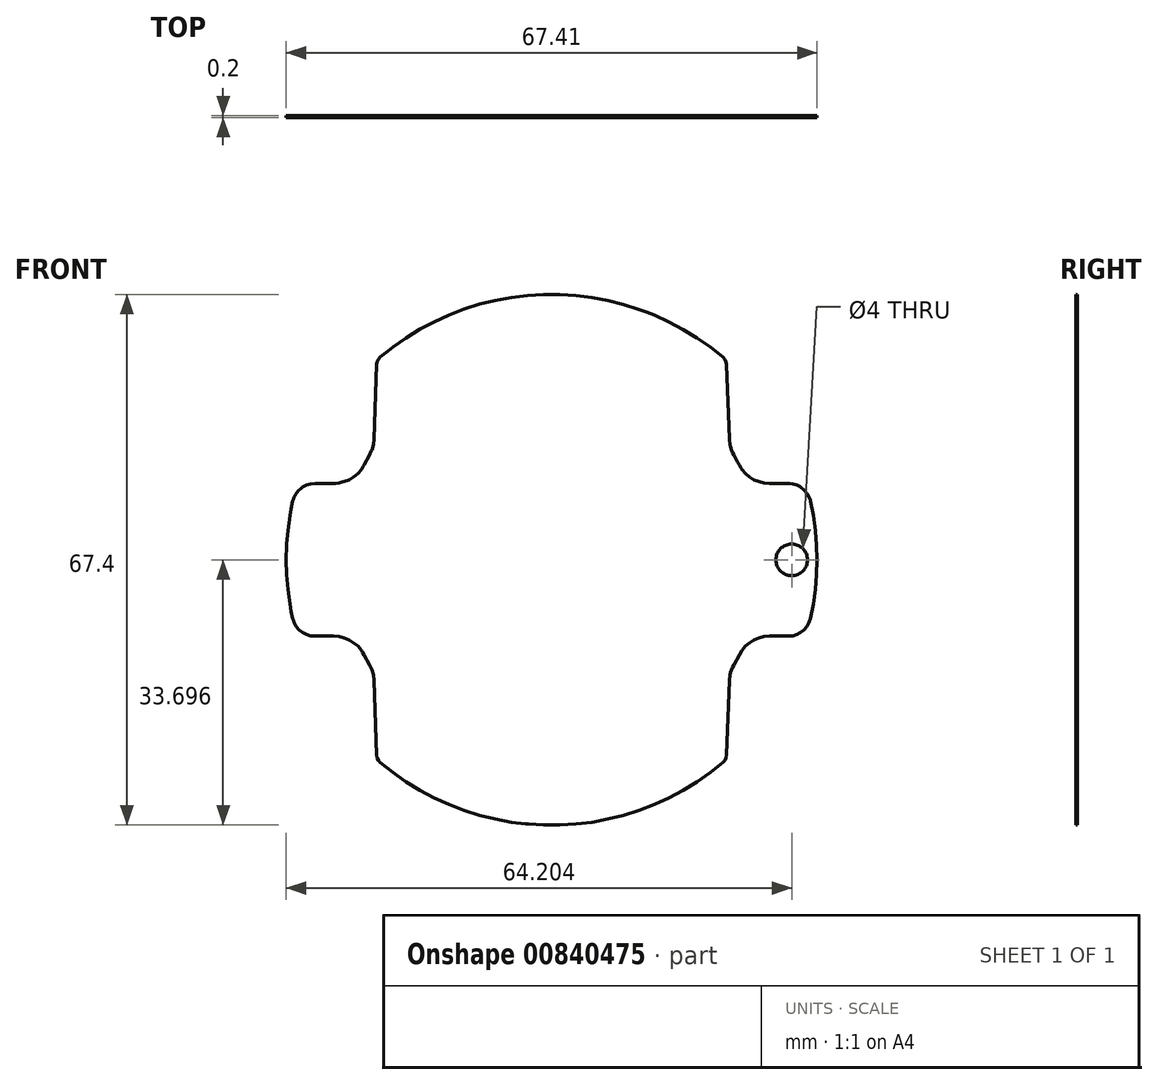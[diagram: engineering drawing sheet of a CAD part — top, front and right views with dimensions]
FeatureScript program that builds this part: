
annotation { "Feature Type Name" : "Feature", "Feature Type Description" : "" }
export const myFeature = defineFeature(function(context is Context, id is Id, definition is map)
    precondition{}
    {
        {
            var Q0;
            Q0=qCreatedBy(makeId("Front.planeOp"),FACE);
            var sketch = newSketch(context, id + "F0", { "sketchPlane" : qUnion([Q0])});
            skFitSpline(sketch, "E0.0.0", {"points": [v(23.84, -14.54) * mm, v(23.9, -14.43) * mm, v(23.95, -14.32) * mm, v(24, -14.2) * mm]});
            skFitSpline(sketch, "E0.0.1", {"points": [v(24, -14.2) * mm, v(24.24, -13.78) * mm, v(24.47, -13.36) * mm, v(24.7, -12.93) * mm]});
            skFitSpline(sketch, "E0.0.2", {"points": [v(24.7, -12.93) * mm, v(24.81, -12.74) * mm, v(24.92, -12.55) * mm, v(25.04, -12.36) * mm]});
            skFitSpline(sketch, "E0.0.3", {"points": [v(25.04, -12.36) * mm, v(25.18, -12.19) * mm, v(25.33, -12) * mm, v(25.47, -11.83) * mm]});
            skFitSpline(sketch, "E0.0.4", {"points": [v(25.47, -11.83) * mm, v(25.65, -11.69) * mm, v(25.83, -11.54) * mm, v(26, -11.4) * mm]});
            skFitSpline(sketch, "E0.0.5", {"points": [v(26, -11.4) * mm, v(26.2, -11.27) * mm, v(26.39, -11.15) * mm, v(26.58, -11.03) * mm]});
            skFitSpline(sketch, "E0.0.6", {"points": [v(26.58, -11.03) * mm, v(26.79, -10.95) * mm, v(27, -10.87) * mm, v(27.21, -10.8) * mm]});
            skFitSpline(sketch, "E0.0.7", {"points": [v(27.21, -10.8) * mm, v(27.42, -10.74) * mm, v(27.64, -10.68) * mm, v(27.85, -10.63) * mm]});
            skFitSpline(sketch, "E0.0.8", {"points": [v(27.85, -10.63) * mm, v(28.08, -10.6) * mm, v(28.32, -10.58) * mm, v(28.55, -10.56) * mm]});
            skFitSpline(sketch, "E0.0.9", {"points": [v(28.55, -10.56) * mm, v(29.34, -10.56) * mm, v(30.13, -10.56) * mm, v(30.92, -10.56) * mm]});
            skFitSpline(sketch, "E0.0.10", {"points": [v(30.92, -10.56) * mm, v(31.11, -10.55) * mm, v(31.3, -10.54) * mm, v(31.5, -10.53) * mm]});
            skFitSpline(sketch, "E0.0.11", {"points": [v(31.5, -10.53) * mm, v(31.67, -10.47) * mm, v(31.85, -10.42) * mm, v(32.03, -10.36) * mm]});
            skFitSpline(sketch, "E0.0.12", {"points": [v(32.03, -10.36) * mm, v(32.18, -10.27) * mm, v(32.34, -10.18) * mm, v(32.5, -10.1) * mm]});
            skFitSpline(sketch, "E0.0.13", {"points": [v(32.5, -10.1) * mm, v(32.64, -9.98) * mm, v(32.79, -9.87) * mm, v(32.93, -9.76) * mm]});
            skFitSpline(sketch, "E0.0.14", {"points": [v(32.93, -9.76) * mm, v(33.05, -9.61) * mm, v(33.18, -9.47) * mm, v(33.3, -9.32) * mm]});
            skFitSpline(sketch, "E0.0.15", {"points": [v(33.3, -9.32) * mm, v(33.39, -9.16) * mm, v(33.48, -8.99) * mm, v(33.57, -8.82) * mm]});
            skFitSpline(sketch, "E0.0.16", {"points": [v(33.57, -8.82) * mm, v(33.63, -8.66) * mm, v(33.7, -8.49) * mm, v(33.77, -8.32) * mm]});
            skFitSpline(sketch, "E0.0.17", {"points": [v(33.77, -8.32) * mm, v(33.88, -7.7) * mm, v(33.99, -7.1) * mm, v(34.1, -6.48) * mm]});
            skFitSpline(sketch, "E0.0.18", {"points": [v(34.1, -6.48) * mm, v(34.19, -5.86) * mm, v(34.28, -5.23) * mm, v(34.37, -4.6) * mm]});
            skFitSpline(sketch, "E0.0.19", {"points": [v(34.37, -4.6) * mm, v(34.42, -3.99) * mm, v(34.48, -3.36) * mm, v(34.53, -2.74) * mm]});
            skFitSpline(sketch, "E0.0.20", {"points": [v(34.53, -2.74) * mm, v(34.55, -2.11) * mm, v(34.56, -1.49) * mm, v(34.57, -0.87) * mm]});
            skFitSpline(sketch, "E0.0.21", {"points": [v(34.57, -0.87) * mm, v(34.56, -0.24) * mm, v(34.55, 0.38) * mm, v(34.53, 1) * mm]});
            skFitSpline(sketch, "E0.0.22", {"points": [v(34.53, 1) * mm, v(34.48, 1.58) * mm, v(34.43, 2.15) * mm, v(34.38, 2.73) * mm]});
            skFitSpline(sketch, "E0.0.23", {"points": [v(34.38, 2.73) * mm, v(34.38, 2.78) * mm, v(34.37, 2.83) * mm, v(34.37, 2.88) * mm]});
            skFitSpline(sketch, "E0.0.24", {"points": [v(34.37, 2.88) * mm, v(34.28, 3.5) * mm, v(34.2, 4.13) * mm, v(34.1, 4.75) * mm]});
            skFitSpline(sketch, "E0.0.25", {"points": [v(34.1, 4.75) * mm, v(33.99, 5.36) * mm, v(33.88, 5.98) * mm, v(33.77, 6.6) * mm]});
            skFitSpline(sketch, "E0.0.26", {"points": [v(33.77, 6.6) * mm, v(33.75, 6.63) * mm, v(33.73, 6.67) * mm, v(33.72, 6.71) * mm]});
            skFitSpline(sketch, "E0.0.27", {"points": [v(33.72, 6.71) * mm, v(33.67, 6.84) * mm, v(33.62, 6.97) * mm, v(33.57, 7.1) * mm]});
            skFitSpline(sketch, "E0.0.28", {"points": [v(33.57, 7.1) * mm, v(33.48, 7.26) * mm, v(33.39, 7.43) * mm, v(33.3, 7.6) * mm]});
            skFitSpline(sketch, "E0.0.29", {"points": [v(33.3, 7.6) * mm, v(33.18, 7.74) * mm, v(33.05, 7.88) * mm, v(32.93, 8.03) * mm]});
            skFitSpline(sketch, "E0.0.30", {"points": [v(32.93, 8.03) * mm, v(32.79, 8.14) * mm, v(32.64, 8.25) * mm, v(32.5, 8.36) * mm]});
            skFitSpline(sketch, "E0.0.31", {"points": [v(32.5, 8.36) * mm, v(32.46, 8.38) * mm, v(32.42, 8.4) * mm, v(32.39, 8.43) * mm]});
            skFitSpline(sketch, "E0.0.32", {"points": [v(32.39, 8.43) * mm, v(32.27, 8.5) * mm, v(32.15, 8.56) * mm, v(32.03, 8.63) * mm]});
            skFitSpline(sketch, "E0.0.33", {"points": [v(32.03, 8.63) * mm, v(31.94, 8.66) * mm, v(31.86, 8.68) * mm, v(31.77, 8.7) * mm]});
            skFitSpline(sketch, "E0.0.34", {"points": [v(31.77, 8.7) * mm, v(31.68, 8.74) * mm, v(31.59, 8.77) * mm, v(31.5, 8.8) * mm]});
            skFitSpline(sketch, "E0.0.35", {"points": [v(31.5, 8.8) * mm, v(31.38, 8.8) * mm, v(31.26, 8.81) * mm, v(31.14, 8.82) * mm]});
            skFitSpline(sketch, "E0.0.36", {"points": [v(31.14, 8.82) * mm, v(31.07, 8.82) * mm, v(31, 8.83) * mm, v(30.92, 8.83) * mm]});
            skFitSpline(sketch, "E0.0.37", {"points": [v(30.92, 8.83) * mm, v(30.13, 8.83) * mm, v(29.34, 8.83) * mm, v(28.55, 8.83) * mm]});
            skFitSpline(sketch, "E0.0.38", {"points": [v(28.55, 8.83) * mm, v(28.32, 8.85) * mm, v(28.08, 8.88) * mm, v(27.85, 8.9) * mm]});
            skFitSpline(sketch, "E0.0.39", {"points": [v(27.85, 8.9) * mm, v(27.64, 8.95) * mm, v(27.43, 9) * mm, v(27.21, 9.06) * mm]});
            skFitSpline(sketch, "E0.0.40", {"points": [v(27.21, 9.06) * mm, v(27, 9.14) * mm, v(26.8, 9.22) * mm, v(26.58, 9.3) * mm]});
            skFitSpline(sketch, "E0.0.41", {"points": [v(26.58, 9.3) * mm, v(26.39, 9.42) * mm, v(26.2, 9.54) * mm, v(26, 9.67) * mm]});
            skFitSpline(sketch, "E0.0.42", {"points": [v(26, 9.67) * mm, v(25.83, 9.81) * mm, v(25.65, 9.96) * mm, v(25.47, 10.1) * mm]});
            skFitSpline(sketch, "E0.0.43", {"points": [v(25.47, 10.1) * mm, v(25.33, 10.28) * mm, v(25.18, 10.46) * mm, v(25.04, 10.64) * mm]});
            skFitSpline(sketch, "E0.0.44", {"points": [v(25.04, 10.64) * mm, v(25, 10.7) * mm, v(24.96, 10.76) * mm, v(24.93, 10.82) * mm]});
            skFitSpline(sketch, "E0.0.45", {"points": [v(24.93, 10.82) * mm, v(24.85, 10.95) * mm, v(24.78, 11.08) * mm, v(24.7, 11.2) * mm]});
            skFitSpline(sketch, "E0.0.46", {"points": [v(24.7, 11.2) * mm, v(24.63, 11.33) * mm, v(24.56, 11.46) * mm, v(24.5, 11.59) * mm]});
            skFitSpline(sketch, "E0.0.47", {"points": [v(24.5, 11.59) * mm, v(24.33, 11.88) * mm, v(24.17, 12.18) * mm, v(24, 12.47) * mm]});
            skFitSpline(sketch, "E0.0.48", {"points": [v(24, 12.47) * mm, v(23.95, 12.58) * mm, v(23.9, 12.68) * mm, v(23.86, 12.78) * mm]});
            skFitSpline(sketch, "E0.0.49", {"points": [v(23.86, 12.78) * mm, v(23.8, 12.89) * mm, v(23.75, 13) * mm, v(23.7, 13.1) * mm]});
            skFitSpline(sketch, "E0.0.50", {"points": [v(23.7, 13.1) * mm, v(23.66, 13.25) * mm, v(23.61, 13.39) * mm, v(23.57, 13.53) * mm]});
            skFitSpline(sketch, "E0.0.51", {"points": [v(23.57, 13.53) * mm, v(23.55, 13.61) * mm, v(23.52, 13.7) * mm, v(23.5, 13.78) * mm]});
            skFitSpline(sketch, "E0.0.52", {"points": [v(23.5, 13.78) * mm, v(23.48, 14) * mm, v(23.46, 14.2) * mm, v(23.44, 14.41) * mm]});
            skFitSpline(sketch, "E0.0.53", {"points": [v(23.44, 14.41) * mm, v(23.44, 14.44) * mm, v(23.43, 14.46) * mm, v(23.43, 14.48) * mm]});
            skFitSpline(sketch, "E0.0.54", {"points": [v(23.43, 14.48) * mm, v(23.32, 17.64) * mm, v(23.21, 20.79) * mm, v(23.1, 23.94) * mm]});
            skFitSpline(sketch, "E0.0.55", {"points": [v(23.1, 23.94) * mm, v(23.08, 24.05) * mm, v(23.05, 24.17) * mm, v(23.03, 24.28) * mm]});
            skFitSpline(sketch, "E0.0.56", {"points": [v(23.03, 24.28) * mm, v(22.98, 24.39) * mm, v(22.92, 24.5) * mm, v(22.86, 24.61) * mm]});
            skFitSpline(sketch, "E0.0.57", {"points": [v(22.86, 24.61) * mm, v(22.79, 24.7) * mm, v(22.7, 24.79) * mm, v(22.63, 24.88) * mm]});
            skFitSpline(sketch, "E0.0.58", {"points": [v(22.63, 24.88) * mm, v(22.1, 25.3) * mm, v(21.56, 25.72) * mm, v(21.03, 26.15) * mm]});
            skFitSpline(sketch, "E0.0.59", {"points": [v(21.03, 26.15) * mm, v(20.47, 26.54) * mm, v(19.91, 26.93) * mm, v(19.35, 27.32) * mm]});
            skFitSpline(sketch, "E0.0.60", {"points": [v(19.35, 27.32) * mm, v(18.76, 27.69) * mm, v(18.17, 28.06) * mm, v(17.58, 28.42) * mm]});
            skFitSpline(sketch, "E0.0.61", {"points": [v(17.58, 28.42) * mm, v(16.98, 28.74) * mm, v(16.38, 29.05) * mm, v(15.78, 29.36) * mm]});
            skFitSpline(sketch, "E0.0.62", {"points": [v(15.78, 29.36) * mm, v(15.15, 29.65) * mm, v(14.53, 29.94) * mm, v(13.9, 30.23) * mm]});
            skFitSpline(sketch, "E0.0.63", {"points": [v(13.9, 30.23) * mm, v(13.57, 30.36) * mm, v(13.23, 30.48) * mm, v(12.9, 30.61) * mm]});
            skFitSpline(sketch, "E0.0.64", {"points": [v(12.9, 30.61) * mm, v(12.59, 30.73) * mm, v(12.28, 30.85) * mm, v(11.97, 30.96) * mm]});
            skFitSpline(sketch, "E0.0.65", {"points": [v(11.97, 30.96) * mm, v(11.32, 31.18) * mm, v(10.67, 31.39) * mm, v(10.03, 31.6) * mm]});
            skFitSpline(sketch, "E0.0.66", {"points": [v(10.03, 31.6) * mm, v(9.36, 31.75) * mm, v(8.69, 31.91) * mm, v(8.02, 32.07) * mm]});
            skFitSpline(sketch, "E0.0.67", {"points": [v(8.02, 32.07) * mm, v(7.34, 32.2) * mm, v(6.66, 32.34) * mm, v(5.98, 32.47) * mm]});
            skFitSpline(sketch, "E0.0.68", {"points": [v(5.98, 32.47) * mm, v(5.3, 32.55) * mm, v(4.62, 32.63) * mm, v(3.94, 32.7) * mm]});
            skFitSpline(sketch, "E0.0.69", {"points": [v(3.94, 32.7) * mm, v(3.26, 32.75) * mm, v(2.58, 32.8) * mm, v(1.9, 32.84) * mm]});
            skFitSpline(sketch, "E0.0.70", {"points": [v(1.9, 32.84) * mm, v(1.21, 32.84) * mm, v(0.52, 32.84) * mm, v(-0.17, 32.84) * mm]});
            skFitSpline(sketch, "E0.0.71", {"points": [v(-0.17, 32.84) * mm, v(-0.85, 32.8) * mm, v(-1.53, 32.75) * mm, v(-2.21, 32.7) * mm]});
            skFitSpline(sketch, "E0.0.72", {"points": [v(-2.21, 32.7) * mm, v(-2.9, 32.63) * mm, v(-3.57, 32.55) * mm, v(-4.25, 32.47) * mm]});
            skFitSpline(sketch, "E0.0.73", {"points": [v(-4.25, 32.47) * mm, v(-4.93, 32.34) * mm, v(-5.61, 32.2) * mm, v(-6.29, 32.07) * mm]});
            skFitSpline(sketch, "E0.0.74", {"points": [v(-6.29, 32.07) * mm, v(-6.96, 31.91) * mm, v(-7.63, 31.76) * mm, v(-8.3, 31.6) * mm]});
            skFitSpline(sketch, "E0.0.75", {"points": [v(-8.3, 31.6) * mm, v(-8.94, 31.39) * mm, v(-9.59, 31.18) * mm, v(-10.23, 30.96) * mm]});
            skFitSpline(sketch, "E0.0.76", {"points": [v(-10.23, 30.96) * mm, v(-10.46, 30.88) * mm, v(-10.68, 30.8) * mm, v(-10.9, 30.71) * mm]});
            skFitSpline(sketch, "E0.0.77", {"points": [v(-10.9, 30.71) * mm, v(-11.33, 30.55) * mm, v(-11.75, 30.4) * mm, v(-12.17, 30.23) * mm]});
            skFitSpline(sketch, "E0.0.78", {"points": [v(-12.17, 30.23) * mm, v(-12.8, 29.94) * mm, v(-13.42, 29.65) * mm, v(-14.05, 29.36) * mm]});
            skFitSpline(sketch, "E0.0.79", {"points": [v(-14.05, 29.36) * mm, v(-14.65, 29.05) * mm, v(-15.25, 28.74) * mm, v(-15.85, 28.42) * mm]});
            skFitSpline(sketch, "E0.0.80", {"points": [v(-15.85, 28.42) * mm, v(-16.44, 28.06) * mm, v(-17.03, 27.69) * mm, v(-17.62, 27.32) * mm]});
            skFitSpline(sketch, "E0.0.81", {"points": [v(-17.62, 27.32) * mm, v(-18.18, 26.93) * mm, v(-18.74, 26.54) * mm, v(-19.3, 26.15) * mm]});
            skFitSpline(sketch, "E0.0.82", {"points": [v(-19.3, 26.15) * mm, v(-19.5, 25.98) * mm, v(-19.72, 25.81) * mm, v(-19.93, 25.64) * mm]});
            skFitSpline(sketch, "E0.0.83", {"points": [v(-19.93, 25.64) * mm, v(-20.26, 25.39) * mm, v(-20.58, 25.13) * mm, v(-20.9, 24.88) * mm]});
            skFitSpline(sketch, "E0.0.84", {"points": [v(-20.9, 24.88) * mm, v(-20.95, 24.82) * mm, v(-21, 24.76) * mm, v(-21.05, 24.7) * mm]});
            skFitSpline(sketch, "E0.0.85", {"points": [v(-21.05, 24.7) * mm, v(-21.08, 24.68) * mm, v(-21.1, 24.65) * mm, v(-21.14, 24.61) * mm]});
            skFitSpline(sketch, "E0.0.86", {"points": [v(-21.14, 24.61) * mm, v(-21.2, 24.5) * mm, v(-21.25, 24.4) * mm, v(-21.3, 24.28) * mm]});
            skFitSpline(sketch, "E0.0.87", {"points": [v(-21.3, 24.28) * mm, v(-21.32, 24.17) * mm, v(-21.35, 24.06) * mm, v(-21.37, 23.94) * mm]});
            skFitSpline(sketch, "E0.0.88", {"points": [v(-21.37, 23.94) * mm, v(-21.48, 20.8) * mm, v(-21.6, 17.64) * mm, v(-21.7, 14.48) * mm]});
            skFitSpline(sketch, "E0.0.89", {"points": [v(-21.7, 14.48) * mm, v(-21.73, 14.25) * mm, v(-21.75, 14.01) * mm, v(-21.77, 13.78) * mm]});
            skFitSpline(sketch, "E0.0.90", {"points": [v(-21.77, 13.78) * mm, v(-21.84, 13.56) * mm, v(-21.9, 13.33) * mm, v(-21.97, 13.11) * mm]});
            skFitSpline(sketch, "E0.0.91", {"points": [v(-21.97, 13.11) * mm, v(-22, 13.06) * mm, v(-22.02, 13) * mm, v(-22.04, 12.96) * mm]});
            skFitSpline(sketch, "E0.0.92", {"points": [v(-22.04, 12.96) * mm, v(-22.12, 12.8) * mm, v(-22.2, 12.64) * mm, v(-22.27, 12.48) * mm]});
            skFitSpline(sketch, "E0.0.93", {"points": [v(-22.27, 12.48) * mm, v(-22.5, 12.05) * mm, v(-22.74, 11.63) * mm, v(-22.97, 11.2) * mm]});
            skFitSpline(sketch, "E0.0.94", {"points": [v(-22.97, 11.2) * mm, v(-23.02, 11.13) * mm, v(-23.06, 11.05) * mm, v(-23.11, 10.97) * mm]});
            skFitSpline(sketch, "E0.0.95", {"points": [v(-23.11, 10.97) * mm, v(-23.18, 10.86) * mm, v(-23.24, 10.75) * mm, v(-23.3, 10.64) * mm]});
            skFitSpline(sketch, "E0.0.96", {"points": [v(-23.3, 10.64) * mm, v(-23.45, 10.46) * mm, v(-23.6, 10.28) * mm, v(-23.74, 10.1) * mm]});
            skFitSpline(sketch, "E0.0.97", {"points": [v(-23.74, 10.1) * mm, v(-23.83, 10.03) * mm, v(-23.92, 9.95) * mm, v(-24.01, 9.88) * mm]});
            skFitSpline(sketch, "E0.0.98", {"points": [v(-24.01, 9.88) * mm, v(-24.1, 9.8) * mm, v(-24.19, 9.74) * mm, v(-24.28, 9.67) * mm]});
            skFitSpline(sketch, "E0.0.99", {"points": [v(-24.28, 9.67) * mm, v(-24.47, 9.54) * mm, v(-24.66, 9.42) * mm, v(-24.85, 9.3) * mm]});
            skFitSpline(sketch, "E0.0.100", {"points": [v(-24.85, 9.3) * mm, v(-25.06, 9.22) * mm, v(-25.27, 9.14) * mm, v(-25.48, 9.07) * mm]});
            skFitSpline(sketch, "E0.0.101", {"points": [v(-25.48, 9.07) * mm, v(-25.57, 9.04) * mm, v(-25.66, 9.02) * mm, v(-25.75, 9) * mm]});
            skFitSpline(sketch, "E0.0.102", {"points": [v(-25.75, 9) * mm, v(-25.87, 8.96) * mm, v(-26, 8.93) * mm, v(-26.12, 8.9) * mm]});
            skFitSpline(sketch, "E0.0.103", {"points": [v(-26.12, 8.9) * mm, v(-26.27, 8.88) * mm, v(-26.42, 8.87) * mm, v(-26.56, 8.86) * mm]});
            skFitSpline(sketch, "E0.0.104", {"points": [v(-26.56, 8.86) * mm, v(-26.65, 8.85) * mm, v(-26.73, 8.84) * mm, v(-26.82, 8.83) * mm]});
            skFitSpline(sketch, "E0.0.105", {"points": [v(-26.82, 8.83) * mm, v(-27.6, 8.83) * mm, v(-28.4, 8.83) * mm, v(-29.2, 8.83) * mm]});
            skFitSpline(sketch, "E0.0.106", {"points": [v(-29.2, 8.83) * mm, v(-29.38, 8.82) * mm, v(-29.57, 8.8) * mm, v(-29.76, 8.8) * mm]});
            skFitSpline(sketch, "E0.0.107", {"points": [v(-29.76, 8.8) * mm, v(-29.94, 8.74) * mm, v(-30.12, 8.69) * mm, v(-30.3, 8.63) * mm]});
            skFitSpline(sketch, "E0.0.108", {"points": [v(-30.3, 8.63) * mm, v(-30.45, 8.54) * mm, v(-30.6, 8.45) * mm, v(-30.76, 8.36) * mm]});
            skFitSpline(sketch, "E0.0.109", {"points": [v(-30.76, 8.36) * mm, v(-30.86, 8.3) * mm, v(-30.95, 8.22) * mm, v(-31.05, 8.14) * mm]});
            skFitSpline(sketch, "E0.0.110", {"points": [v(-31.05, 8.14) * mm, v(-31.1, 8.1) * mm, v(-31.15, 8.07) * mm, v(-31.2, 8.03) * mm]});
            skFitSpline(sketch, "E0.0.111", {"points": [v(-31.2, 8.03) * mm, v(-31.32, 7.89) * mm, v(-31.44, 7.74) * mm, v(-31.57, 7.6) * mm]});
            skFitSpline(sketch, "E0.0.112", {"points": [v(-31.57, 7.6) * mm, v(-31.58, 7.57) * mm, v(-31.6, 7.54) * mm, v(-31.61, 7.5) * mm]});
            skFitSpline(sketch, "E0.0.113", {"points": [v(-31.61, 7.5) * mm, v(-31.69, 7.37) * mm, v(-31.76, 7.23) * mm, v(-31.83, 7.1) * mm]});
            skFitSpline(sketch, "E0.0.114", {"points": [v(-31.83, 7.1) * mm, v(-31.86, 7.02) * mm, v(-31.9, 6.94) * mm, v(-31.93, 6.86) * mm]});
            skFitSpline(sketch, "E0.0.115", {"points": [v(-31.93, 6.86) * mm, v(-31.96, 6.77) * mm, v(-32, 6.68) * mm, v(-32.03, 6.6) * mm]});
            skFitSpline(sketch, "E0.0.116", {"points": [v(-32.03, 6.6) * mm, v(-32.1, 6.26) * mm, v(-32.15, 5.94) * mm, v(-32.21, 5.6) * mm]});
            skFitSpline(sketch, "E0.0.117", {"points": [v(-32.21, 5.6) * mm, v(-32.27, 5.32) * mm, v(-32.32, 5.04) * mm, v(-32.37, 4.75) * mm]});
            skFitSpline(sketch, "E0.0.118", {"points": [v(-32.37, 4.75) * mm, v(-32.41, 4.45) * mm, v(-32.46, 4.15) * mm, v(-32.5, 3.84) * mm]});
            skFitSpline(sketch, "E0.0.119", {"points": [v(-32.5, 3.84) * mm, v(-32.54, 3.52) * mm, v(-32.6, 3.2) * mm, v(-32.64, 2.88) * mm]});
            skFitSpline(sketch, "E0.0.120", {"points": [v(-32.64, 2.88) * mm, v(-32.69, 2.3) * mm, v(-32.74, 1.72) * mm, v(-32.8, 1.13) * mm]});
            skFitSpline(sketch, "E0.0.121", {"points": [v(-32.8, 1.13) * mm, v(-32.8, 1.1) * mm, v(-32.8, 1.05) * mm, v(-32.8, 1) * mm]});
            skFitSpline(sketch, "E0.0.122", {"points": [v(-32.8, 1) * mm, v(-32.81, 0.38) * mm, v(-32.83, -0.24) * mm, v(-32.84, -0.86) * mm]});
            skFitSpline(sketch, "E0.0.123", {"points": [v(-32.84, -0.86) * mm, v(-32.83, -1.49) * mm, v(-32.81, -2.11) * mm, v(-32.8, -2.74) * mm]});
            skFitSpline(sketch, "E0.0.124", {"points": [v(-32.8, -2.74) * mm, v(-32.75, -3.36) * mm, v(-32.7, -3.98) * mm, v(-32.64, -4.6) * mm]});
            skFitSpline(sketch, "E0.0.125", {"points": [v(-32.64, -4.6) * mm, v(-32.59, -4.94) * mm, v(-32.54, -5.27) * mm, v(-32.5, -5.6) * mm]});
            skFitSpline(sketch, "E0.0.126", {"points": [v(-32.5, -5.6) * mm, v(-32.45, -5.9) * mm, v(-32.41, -6.19) * mm, v(-32.37, -6.48) * mm]});
            skFitSpline(sketch, "E0.0.127", {"points": [v(-32.37, -6.48) * mm, v(-32.31, -6.79) * mm, v(-32.26, -7.1) * mm, v(-32.2, -7.4) * mm]});
            skFitSpline(sketch, "E0.0.128", {"points": [v(-32.2, -7.4) * mm, v(-32.15, -7.7) * mm, v(-32.1, -8.01) * mm, v(-32.03, -8.32) * mm]});
            skFitSpline(sketch, "E0.0.129", {"points": [v(-32.03, -8.32) * mm, v(-32, -8.4) * mm, v(-31.97, -8.49) * mm, v(-31.93, -8.57) * mm]});
            skFitSpline(sketch, "E0.0.130", {"points": [v(-31.93, -8.57) * mm, v(-31.9, -8.65) * mm, v(-31.87, -8.74) * mm, v(-31.83, -8.82) * mm]});
            skFitSpline(sketch, "E0.0.131", {"points": [v(-31.83, -8.82) * mm, v(-31.75, -8.99) * mm, v(-31.66, -9.15) * mm, v(-31.57, -9.32) * mm]});
            skFitSpline(sketch, "E0.0.132", {"points": [v(-31.57, -9.32) * mm, v(-31.44, -9.47) * mm, v(-31.32, -9.61) * mm, v(-31.2, -9.76) * mm]});
            skFitSpline(sketch, "E0.0.133", {"points": [v(-31.2, -9.76) * mm, v(-31.05, -9.87) * mm, v(-30.9, -9.98) * mm, v(-30.76, -10.1) * mm]});
            skFitSpline(sketch, "E0.0.134", {"points": [v(-30.76, -10.1) * mm, v(-30.6, -10.18) * mm, v(-30.45, -10.27) * mm, v(-30.3, -10.36) * mm]});
            skFitSpline(sketch, "E0.0.135", {"points": [v(-30.3, -10.36) * mm, v(-30.12, -10.41) * mm, v(-29.94, -10.47) * mm, v(-29.76, -10.53) * mm]});
            skFitSpline(sketch, "E0.0.136", {"points": [v(-29.76, -10.53) * mm, v(-29.57, -10.54) * mm, v(-29.38, -10.55) * mm, v(-29.2, -10.56) * mm]});
            skFitSpline(sketch, "E0.0.137", {"points": [v(-29.2, -10.56) * mm, v(-28.4, -10.56) * mm, v(-27.61, -10.56) * mm, v(-26.82, -10.56) * mm]});
            skFitSpline(sketch, "E0.0.138", {"points": [v(-26.82, -10.56) * mm, v(-26.59, -10.58) * mm, v(-26.35, -10.6) * mm, v(-26.12, -10.63) * mm]});
            skFitSpline(sketch, "E0.0.139", {"points": [v(-26.12, -10.63) * mm, v(-25.9, -10.68) * mm, v(-25.7, -10.74) * mm, v(-25.48, -10.8) * mm]});
            skFitSpline(sketch, "E0.0.140", {"points": [v(-25.48, -10.8) * mm, v(-25.27, -10.87) * mm, v(-25.06, -10.95) * mm, v(-24.85, -11.03) * mm]});
            skFitSpline(sketch, "E0.0.141", {"points": [v(-24.85, -11.03) * mm, v(-24.66, -11.15) * mm, v(-24.47, -11.27) * mm, v(-24.28, -11.4) * mm]});
            skFitSpline(sketch, "E0.0.142", {"points": [v(-24.28, -11.4) * mm, v(-24.1, -11.54) * mm, v(-23.92, -11.69) * mm, v(-23.74, -11.83) * mm]});
            skFitSpline(sketch, "E0.0.143", {"points": [v(-23.74, -11.83) * mm, v(-23.6, -12) * mm, v(-23.45, -12.19) * mm, v(-23.3, -12.36) * mm]});
            skFitSpline(sketch, "E0.0.144", {"points": [v(-23.3, -12.36) * mm, v(-23.25, -12.46) * mm, v(-23.2, -12.55) * mm, v(-23.14, -12.65) * mm]});
            skFitSpline(sketch, "E0.0.145", {"points": [v(-23.14, -12.65) * mm, v(-23.09, -12.74) * mm, v(-23.03, -12.84) * mm, v(-22.97, -12.93) * mm]});
            skFitSpline(sketch, "E0.0.146", {"points": [v(-22.97, -12.93) * mm, v(-22.74, -13.36) * mm, v(-22.5, -13.78) * mm, v(-22.27, -14.2) * mm]});
            skFitSpline(sketch, "E0.0.147", {"points": [v(-22.27, -14.2) * mm, v(-22.17, -14.42) * mm, v(-22.07, -14.63) * mm, v(-21.97, -14.84) * mm]});
            skFitSpline(sketch, "E0.0.148", {"points": [v(-21.97, -14.84) * mm, v(-21.9, -15.06) * mm, v(-21.84, -15.28) * mm, v(-21.77, -15.5) * mm]});
            skFitSpline(sketch, "E0.0.149", {"points": [v(-21.77, -15.5) * mm, v(-21.75, -15.74) * mm, v(-21.73, -15.97) * mm, v(-21.7, -16.2) * mm]});
            skFitSpline(sketch, "E0.0.150", {"points": [v(-21.7, -16.2) * mm, v(-21.6, -19.36) * mm, v(-21.48, -22.52) * mm, v(-21.37, -25.67) * mm]});
            skFitSpline(sketch, "E0.0.151", {"points": [v(-21.37, -25.67) * mm, v(-21.35, -25.78) * mm, v(-21.32, -25.9) * mm, v(-21.3, -26) * mm]});
            skFitSpline(sketch, "E0.0.152", {"points": [v(-21.3, -26) * mm, v(-21.25, -26.12) * mm, v(-21.2, -26.23) * mm, v(-21.14, -26.34) * mm]});
            skFitSpline(sketch, "E0.0.153", {"points": [v(-21.14, -26.34) * mm, v(-21.06, -26.43) * mm, v(-20.98, -26.52) * mm, v(-20.9, -26.6) * mm]});
            skFitSpline(sketch, "E0.0.154", {"points": [v(-20.9, -26.6) * mm, v(-20.37, -27.03) * mm, v(-19.83, -27.46) * mm, v(-19.3, -27.88) * mm]});
            skFitSpline(sketch, "E0.0.155", {"points": [v(-19.3, -27.88) * mm, v(-19.13, -28) * mm, v(-18.96, -28.11) * mm, v(-18.8, -28.23) * mm]});
            skFitSpline(sketch, "E0.0.156", {"points": [v(-18.8, -28.23) * mm, v(-18.4, -28.5) * mm, v(-18.02, -28.78) * mm, v(-17.63, -29.05) * mm]});
            skFitSpline(sketch, "E0.0.157", {"points": [v(-17.63, -29.05) * mm, v(-17.04, -29.42) * mm, v(-16.44, -29.78) * mm, v(-15.85, -30.15) * mm]});
            skFitSpline(sketch, "E0.0.158", {"points": [v(-15.85, -30.15) * mm, v(-15.25, -30.46) * mm, v(-14.65, -30.78) * mm, v(-14.05, -31.09) * mm]});
            skFitSpline(sketch, "E0.0.159", {"points": [v(-14.05, -31.09) * mm, v(-13.43, -31.38) * mm, v(-12.8, -31.67) * mm, v(-12.18, -31.96) * mm]});
            skFitSpline(sketch, "E0.0.160", {"points": [v(-12.18, -31.96) * mm, v(-11.53, -32.2) * mm, v(-10.88, -32.45) * mm, v(-10.24, -32.7) * mm]});
            skFitSpline(sketch, "E0.0.161", {"points": [v(-10.24, -32.7) * mm, v(-9.6, -32.9) * mm, v(-8.95, -33.12) * mm, v(-8.3, -33.33) * mm]});
            skFitSpline(sketch, "E0.0.162", {"points": [v(-8.3, -33.33) * mm, v(-7.63, -33.48) * mm, v(-6.96, -33.64) * mm, v(-6.3, -33.8) * mm]});
            skFitSpline(sketch, "E0.0.163", {"points": [v(-6.3, -33.8) * mm, v(-5.61, -33.93) * mm, v(-4.93, -34.06) * mm, v(-4.25, -34.2) * mm]});
            skFitSpline(sketch, "E0.0.164", {"points": [v(-4.25, -34.2) * mm, v(-3.65, -34.27) * mm, v(-3.05, -34.33) * mm, v(-2.45, -34.4) * mm]});
            skFitSpline(sketch, "E0.0.165", {"points": [v(-2.45, -34.4) * mm, v(-2.37, -34.41) * mm, v(-2.3, -34.42) * mm, v(-2.21, -34.43) * mm]});
            skFitSpline(sketch, "E0.0.166", {"points": [v(-2.21, -34.43) * mm, v(-2.17, -34.43) * mm, v(-2.13, -34.44) * mm, v(-2.09, -34.44) * mm]});
            skFitSpline(sketch, "E0.0.167", {"points": [v(-2.09, -34.44) * mm, v(-1.45, -34.48) * mm, v(-0.81, -34.52) * mm, v(-0.18, -34.56) * mm]});
            skFitSpline(sketch, "E0.0.168", {"points": [v(-0.18, -34.56) * mm, v(0.52, -34.56) * mm, v(1.2, -34.56) * mm, v(1.9, -34.56) * mm]});
            skFitSpline(sketch, "E0.0.169", {"points": [v(1.9, -34.56) * mm, v(2.58, -34.52) * mm, v(3.26, -34.48) * mm, v(3.94, -34.43) * mm]});
            skFitSpline(sketch, "E0.0.170", {"points": [v(3.94, -34.43) * mm, v(4.62, -34.35) * mm, v(5.3, -34.28) * mm, v(5.98, -34.2) * mm]});
            skFitSpline(sketch, "E0.0.171", {"points": [v(5.98, -34.2) * mm, v(6.66, -34.06) * mm, v(7.34, -33.93) * mm, v(8.02, -33.8) * mm]});
            skFitSpline(sketch, "E0.0.172", {"points": [v(8.02, -33.8) * mm, v(8.69, -33.64) * mm, v(9.35, -33.48) * mm, v(10.02, -33.33) * mm]});
            skFitSpline(sketch, "E0.0.173", {"points": [v(10.02, -33.33) * mm, v(10.67, -33.12) * mm, v(11.32, -32.9) * mm, v(11.96, -32.7) * mm]});
            skFitSpline(sketch, "E0.0.174", {"points": [v(11.96, -32.7) * mm, v(12.6, -32.45) * mm, v(13.26, -32.2) * mm, v(13.9, -31.96) * mm]});
            skFitSpline(sketch, "E0.0.175", {"points": [v(13.9, -31.96) * mm, v(14.53, -31.67) * mm, v(15.15, -31.38) * mm, v(15.77, -31.1) * mm]});
            skFitSpline(sketch, "E0.0.176", {"points": [v(15.77, -31.1) * mm, v(16.38, -30.78) * mm, v(16.98, -30.46) * mm, v(17.58, -30.15) * mm]});
            skFitSpline(sketch, "E0.0.177", {"points": [v(17.58, -30.15) * mm, v(18.17, -29.78) * mm, v(18.76, -29.42) * mm, v(19.35, -29.05) * mm]});
            skFitSpline(sketch, "E0.0.178", {"points": [v(19.35, -29.05) * mm, v(19.9, -28.66) * mm, v(20.47, -28.27) * mm, v(21.02, -27.88) * mm]});
            skFitSpline(sketch, "E0.0.179", {"points": [v(21.02, -27.88) * mm, v(21.56, -27.46) * mm, v(22.1, -27.03) * mm, v(22.63, -26.61) * mm]});
            skFitSpline(sketch, "E0.0.180", {"points": [v(22.63, -26.61) * mm, v(22.7, -26.52) * mm, v(22.78, -26.43) * mm, v(22.86, -26.34) * mm]});
            skFitSpline(sketch, "E0.0.181", {"points": [v(22.86, -26.34) * mm, v(22.92, -26.23) * mm, v(22.97, -26.12) * mm, v(23.03, -26) * mm]});
            skFitSpline(sketch, "E0.0.182", {"points": [v(23.03, -26) * mm, v(23.05, -25.9) * mm, v(23.08, -25.78) * mm, v(23.1, -25.67) * mm]});
            skFitSpline(sketch, "E0.0.183", {"points": [v(23.1, -25.67) * mm, v(23.2, -22.52) * mm, v(23.32, -19.36) * mm, v(23.43, -16.2) * mm]});
            skFitSpline(sketch, "E0.0.184", {"points": [v(23.43, -16.2) * mm, v(23.45, -15.98) * mm, v(23.47, -15.74) * mm, v(23.5, -15.5) * mm]});
            skFitSpline(sketch, "E0.0.185", {"points": [v(23.5, -15.5) * mm, v(23.53, -15.39) * mm, v(23.57, -15.27) * mm, v(23.6, -15.15) * mm]});
            skFitSpline(sketch, "E0.0.186", {"points": [v(23.6, -15.15) * mm, v(23.64, -15.05) * mm, v(23.67, -14.94) * mm, v(23.7, -14.84) * mm]});
            skFitSpline(sketch, "E0.0.187", {"points": [v(23.7, -14.84) * mm, v(23.75, -14.74) * mm, v(23.8, -14.64) * mm, v(23.84, -14.54) * mm]});
            skCircle(sketch, "E1.0", {"center": v(31.36, -0.86) * mm, "radius": 2 * mm});
            skSolve(sketch);
        }
        {
            var Q0;
            Q0=makeQuery(id+"F0.imprint","IMPRINT",FACE,{"disambiguationData":[TD([[makeQuery(id+"F0.imprint","IMPRINT",EDGE,{"derivedFrom":sQuery(id+"F0.wireOp",EDGE,"E0.0.0")}),1.0]])]});
            extrude(context, id + "F1", {"entities" : qUnion([Q0]), "oppositeDirection" : true, "depth" : 0.2 * mm, "offsetDistance" : 25 * mm});
        }
    });
